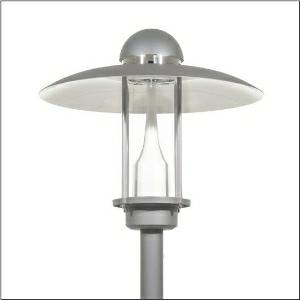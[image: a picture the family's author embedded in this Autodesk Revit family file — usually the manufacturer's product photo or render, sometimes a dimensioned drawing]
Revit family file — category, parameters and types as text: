
# Revit family: city-light_elegance_iq___pl1_2s_5xa5265of14h_1bea
name_source: partatom
category: Lighting Fixtures
units: mm (PartAtom-declared; Revit-internal decimal feet)

## family parameters
Cut with Voids When Loaded = No
Host = Face
Light Source = No
Part Type = Normal
Room Calculation Point = No
Round Connector Dimension = Use Diameter
Shared = No

## types (1)
- --- (1 x LED, 2840 lm, 21.8 W, 2700K)
    Apparent Load = 22 VA
    CIE Flux Codes = 24 63 94 98 100
    Color Rendering = 70
    Color Temperature = 2700K
    Default Elevation = 1800 mm
    Description = City-Light Elegance iQ, mast luminaire, Module 540 iQ-SR, primary light control with 3 zone facetted reflector, of plastic, silver coated, highly specular, structured, primary optical cover: cover, of PMMA, transparent, light distribution: PL1.2s, light emission: direct distribution, primary light characteristic: symmetric, installation type: post-top, LED, High Power LED, rated luminous flux: 2.840lm, luminous efficacy: 130lm/W, light colour: 727, colour temperature: 2700K, control gear: iQ Street-Remote, control: pre-setting: logarithmic dimming characteristic, Street-Remote, Auto-Match, Temp-Guard, Lumen-Switch, Night-Set, Smart-Wire, Light-Fading, Desk-Remote (wireless, voltage-free reading and setting of iQ features in the workshop via application-optimized NFC function/RFID function), optimised constant luminous flux control (CLO 2.0), with terminal, 6-pole, max. 2.5mm², mains connection: 230..240V, AC, 50/60Hz, start of lifetime: 22W, end of service life: 23W, reduction: 11W, luminaire housing, upper part, of aluminium, coated, Siteco® metallic grey (DB 702S), diameter: 750mm, height: 675mm, spigot size: d x l = 76 x 70mm (post-top) | with reducer (optional accessory) 60 x 70mm, mounting height: 3..5m, post-top mast mounting element, of diecast aluminium, coated, Siteco® metallic grey (DB 702S), Module 540 iQ-SR, traffic white (RAL 9016), equipment: standard, protection rating (complete): IP65, insulation class (complete): insulation class II (safety insulation), certification: CE, ENEC, VDE, packaging unit: 1 piece

Light Distribution: PL1.2s
    Height = 675 mm
    Lamp = 1 x LED
    Lamp Light Flux = 2840 lm
    Lamp Power = 21.8 W
    Lamp count = 1
    Length = 750 mm
    Luminous efficacy = 130 lm/W
    Manufacturer = Siteco
    ModVariant = No
    Model = 5XA5265OF14H
    Number of Poles = 1
    OnlyDefault = Yes
    Power Factor = 1
    Product Name = City-Light Elegance iQ | PL1.2s
    Product group = mast luminaire | pylon top
    ProductGroupID = 6100
    Protection Class = Protection class II
    Protection Degree = IP 65
    RLX_Detail_Level = 1
    RLX_Emergency_Light_Flux = 0 lm
    RLX_Emergency_Type = 0
    RLX_Emergency_Type_DB = No
    RlxData = <blob elided: 33537 chars, md5=65c827c3>
    Socket = socket
    Standby Power = 0 W
    System Light Flux = 2840 lm
    System Power = 22 W
    Type Comments = factory setting: luminous flux: 100 % | dim-lin: 254 | 456 mA
    Type Image = l_1006912.jpg
    URL = http://relux.com
    VarID = @adj_166747
    Voltage = 0 V
    Weight = 0.00 kg
    Width = 0 mm  [stored 0 ft]

note: [stored X ft] marks values corroborated as IEEE doubles in the binary element streams (Revit-internal decimal feet)

## geometry (parser evidence)
native form markers: Blend x4, Sweep x9
no freeform markers — native parametric forms only
